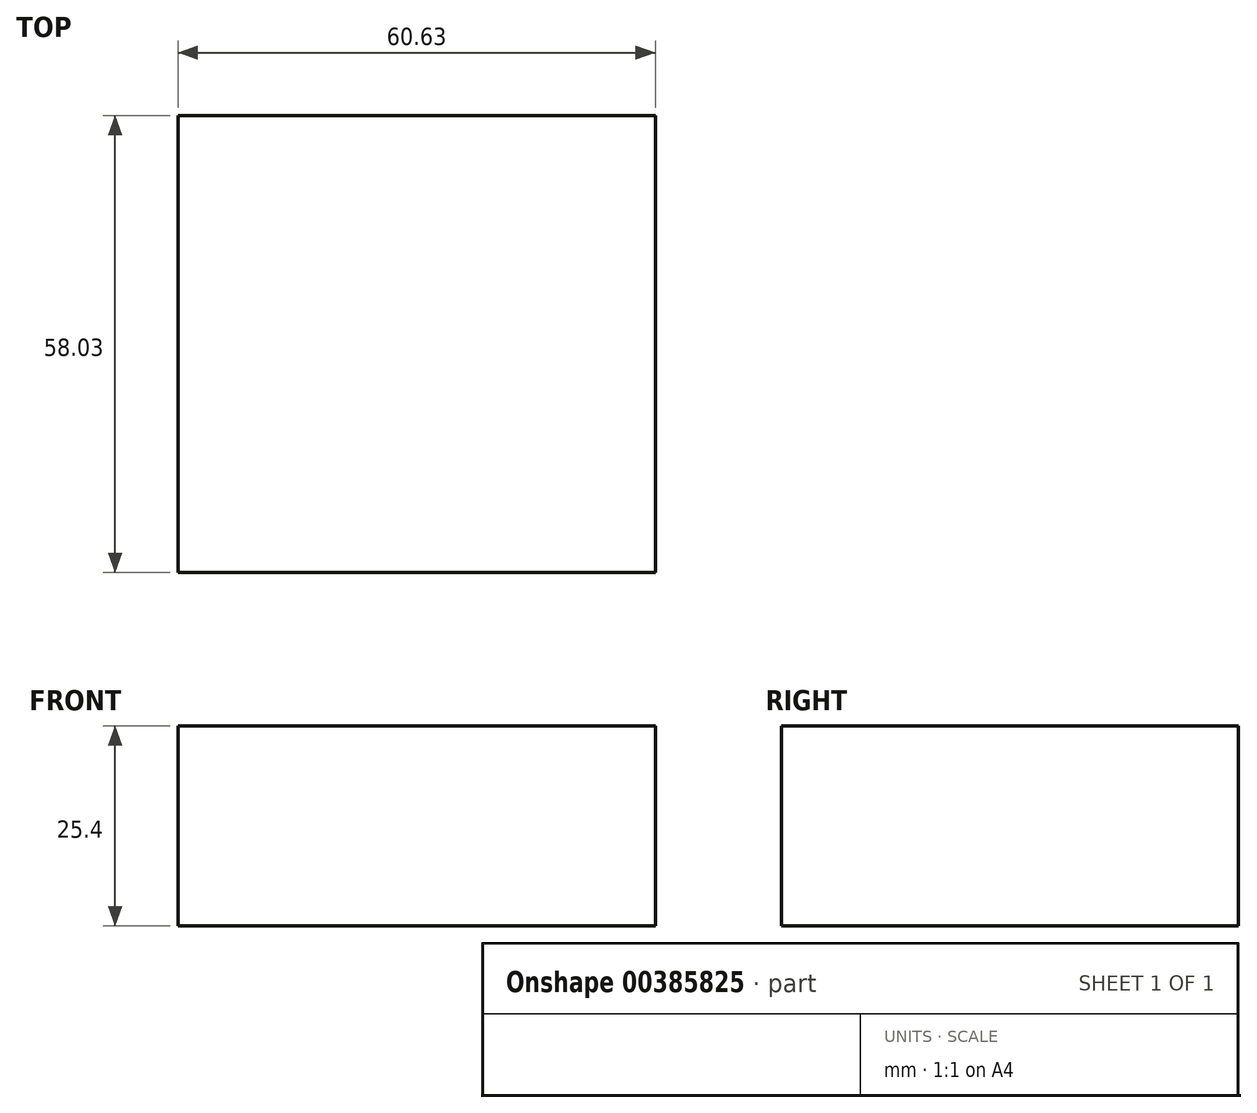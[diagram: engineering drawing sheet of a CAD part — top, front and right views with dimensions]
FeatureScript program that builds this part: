
annotation { "Feature Type Name" : "Feature", "Feature Type Description" : "" }
export const myFeature = defineFeature(function(context is Context, id is Id, definition is map)
    precondition{}
    {
        {
            var Q0;
            Q0=qCreatedBy(makeId("Top.planeOp"),FACE);
            var sketch = newSketch(context, id + "F0", { "sketchPlane" : qUnion([Q0])});
            skLineSegment(sketch, "E0.bottom", {"start": v(-25.98, 35.08) * mm, "end": v(34.65, 35.08) * mm});
            skLineSegment(sketch, "E0.top", {"start": v(-25.98, -22.95) * mm, "end": v(34.65, -22.95) * mm});
            skLineSegment(sketch, "E0.left", {"start": v(-25.98, 35.08) * mm, "end": v(-25.98, -22.95) * mm});
            skLineSegment(sketch, "E0.right", {"start": v(34.65, 35.08) * mm, "end": v(34.65, -22.95) * mm});
            skSolve(sketch);
        }
        {
            var Q0;
            Q0 = qSketchRegion(id + "F0", true);
            extrude(context, id + "F1", {"entities" : qUnion([Q0]), "depth" : 25.4 * mm});
        }
    });
